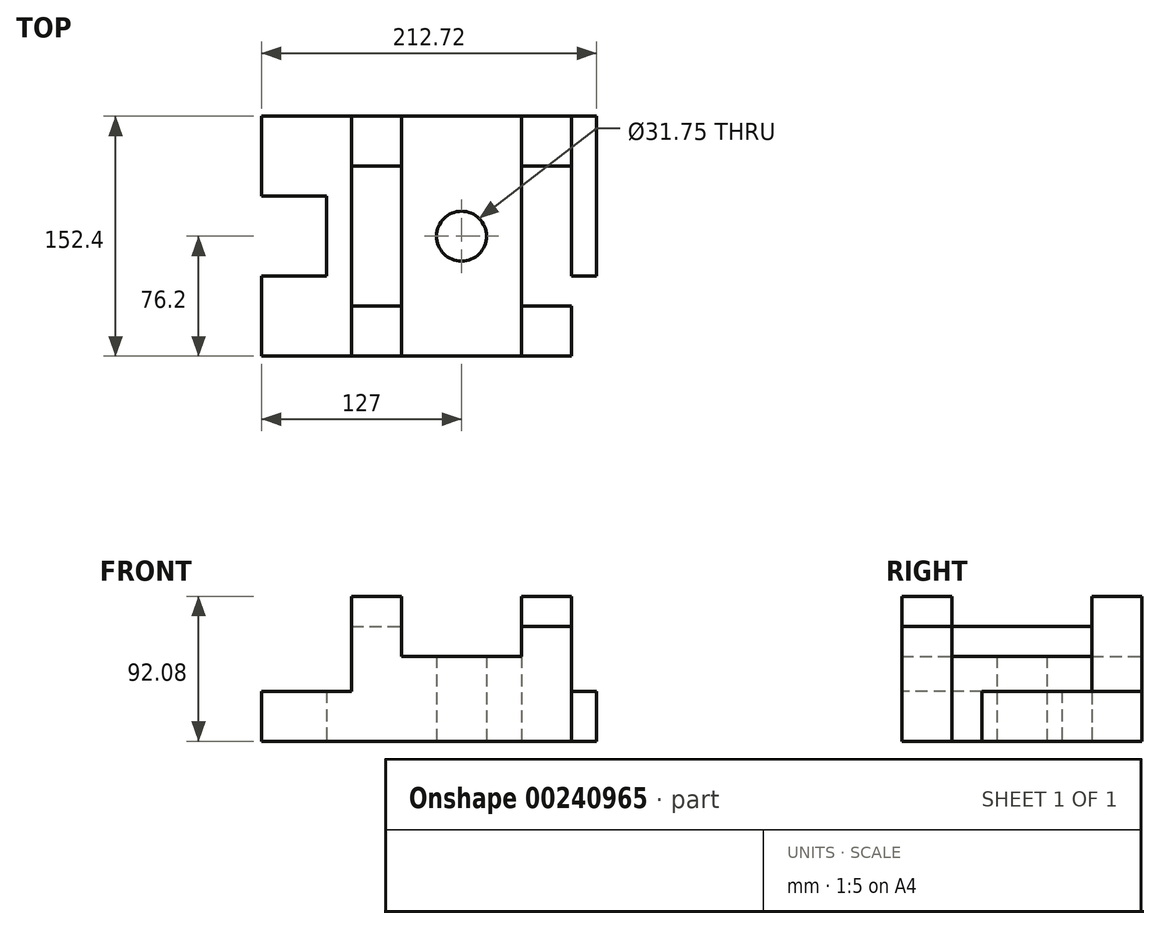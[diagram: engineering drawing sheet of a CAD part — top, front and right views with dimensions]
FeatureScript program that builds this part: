
annotation { "Feature Type Name" : "Feature", "Feature Type Description" : "" }
export const myFeature = defineFeature(function(context is Context, id is Id, definition is map)
    precondition{}
    {
        {
            var Q0;
            Q0=qCreatedBy(makeId("Top.planeOp"),FACE);
            var sketch = newSketch(context, id + "F0", { "sketchPlane" : qUnion([Q0])});
            skLineSegment(sketch, "E0.bottom", {"start": v(-127, 76.2) * mm, "end": v(127, 76.2) * mm});
            skLineSegment(sketch, "E0.top", {"start": v(-127, -76.2) * mm, "end": v(127, -76.2) * mm});
            skLineSegment(sketch, "E0.left", {"start": v(-127, 76.2) * mm, "end": v(-127, -76.2) * mm});
            skLineSegment(sketch, "E0.right", {"start": v(127, 76.2) * mm, "end": v(127, -76.2) * mm});
            skPoint(sketch, "E0.middle", {"position": v(0, 0) * mm});
            skLineSegment(sketch, "E1.bottom", {"start": v(127, -76.2) * mm, "end": v(69.85, -76.2) * mm});
            skLineSegment(sketch, "E1.top", {"start": v(127, -25.4) * mm, "end": v(69.85, -25.4) * mm});
            skLineSegment(sketch, "E1.left", {"start": v(127, -76.2) * mm, "end": v(127, -25.4) * mm});
            skLineSegment(sketch, "E1.right", {"start": v(69.85, -76.2) * mm, "end": v(69.85, -25.4) * mm});
            skLineSegment(sketch, "E2.MirrorCS", {"start": v(85.72, 25.4) * mm, "end": v(85.72, -25.4) * mm});
            skLineSegment(sketch, "E3.MirrorCS", {"start": v(127, 25.1) * mm, "end": v(85.72, 25.4) * mm});
            skLineSegment(sketch, "E4.MirrorCS", {"start": v(127, 25.4) * mm, "end": v(127, -25.4) * mm});
            skLineSegment(sketch, "E5.bottom", {"start": v(85.72, 25.4) * mm, "end": v(69.85, 25.4) * mm});
            skLineSegment(sketch, "E5.top", {"start": v(85.72, 76.2) * mm, "end": v(69.85, 76.2) * mm});
            skLineSegment(sketch, "E5.left", {"start": v(85.72, 25.4) * mm, "end": v(85.72, 76.2) * mm});
            skLineSegment(sketch, "E5.right", {"start": v(69.85, 25.4) * mm, "end": v(69.85, 76.2) * mm});
            skLineSegment(sketch, "E6.MirrorCS", {"start": v(-69.85, 25.4) * mm, "end": v(-69.85, 76.2) * mm});
            skLineSegment(sketch, "E7.MirrorCS", {"start": v(-85.72, 25.4) * mm, "end": v(-69.85, 25.4) * mm});
            skLineSegment(sketch, "E8.MirrorCS", {"start": v(-127, 25.1) * mm, "end": v(-85.72, 25.4) * mm});
            skLineSegment(sketch, "E9.MirrorCS", {"start": v(-85.72, 25.4) * mm, "end": v(-85.72, -25.4) * mm});
            skLineSegment(sketch, "E10.MirrorCS", {"start": v(-127, -25.4) * mm, "end": v(-69.85, -25.4) * mm});
            skLineSegment(sketch, "E11.MirrorCS", {"start": v(-69.85, -76.2) * mm, "end": v(-69.85, -25.4) * mm});
            skLineSegment(sketch, "E12.MirrorCS", {"start": v(-85.72, 25.4) * mm, "end": v(-85.72, 76.2) * mm});
            skLineSegment(sketch, "E13.bottom", {"start": v(69.85, -76.2) * mm, "end": v(38.1, -76.2) * mm});
            skLineSegment(sketch, "E13.top", {"start": v(69.85, -44.45) * mm, "end": v(38.1, -44.45) * mm});
            skLineSegment(sketch, "E13.left", {"start": v(69.85, -76.2) * mm, "end": v(69.85, -44.45) * mm});
            skLineSegment(sketch, "E13.right", {"start": v(38.1, -76.2) * mm, "end": v(38.1, -44.45) * mm});
            skLineSegment(sketch, "E14.MirrorCS", {"start": v(69.85, 44.45) * mm, "end": v(38.1, 44.45) * mm});
            skLineSegment(sketch, "E15.MirrorCS", {"start": v(38.1, 76.2) * mm, "end": v(38.1, 44.45) * mm});
            skLineSegment(sketch, "E16.MirrorCS", {"start": v(-38.1, 76.2) * mm, "end": v(-38.1, 44.45) * mm});
            skLineSegment(sketch, "E17.MirrorCS", {"start": v(-69.85, 44.45) * mm, "end": v(-38.1, 44.45) * mm});
            skLineSegment(sketch, "E18.MirrorCS", {"start": v(-69.85, -44.45) * mm, "end": v(-38.1, -44.45) * mm});
            skLineSegment(sketch, "E19.MirrorCS", {"start": v(-38.1, -76.2) * mm, "end": v(-38.1, -44.45) * mm});
            skLineSegment(sketch, "E20", {"start": v(69.85, 25.4) * mm, "end": v(69.85, -25.4) * mm});
            skLineSegment(sketch, "E21.MirrorCS", {"start": v(-69.85, 25.4) * mm, "end": v(-69.85, -25.4) * mm});
            skLineSegment(sketch, "E22", {"start": v(38.1, 44.45) * mm, "end": v(38.1, -44.45) * mm});
            skLineSegment(sketch, "E23.MirrorCS", {"start": v(-38.1, 44.45) * mm, "end": v(-38.1, -44.45) * mm});
            skCircle(sketch, "E24", {"center": v(0, 0) * mm, "radius": 15.88 * mm});
            skLineSegment(sketch, "E25.bottom", {"start": v(-127, 76.2) * mm, "end": v(-85.72, 76.2) * mm});
            skLineSegment(sketch, "E25.top", {"start": v(-127, 25.4) * mm, "end": v(-85.72, 25.4) * mm});
            skLineSegment(sketch, "E25.left", {"start": v(-127, 76.2) * mm, "end": v(-127, 25.4) * mm});
            skLineSegment(sketch, "E25.right", {"start": v(-85.72, 76.2) * mm, "end": v(-85.72, 25.4) * mm});
            skLineSegment(sketch, "E26.bottom", {"start": v(127, 76.2) * mm, "end": v(85.72, 76.2) * mm});
            skLineSegment(sketch, "E26.top", {"start": v(127, 25.4) * mm, "end": v(85.72, 25.4) * mm});
            skLineSegment(sketch, "E26.left", {"start": v(127, 76.2) * mm, "end": v(127, 25.4) * mm});
            skLineSegment(sketch, "E26.right", {"start": v(85.72, 76.2) * mm, "end": v(85.72, 25.4) * mm});
            skSolve(sketch);
        }
        {
            var Q0;
            {var subQ4=sQuery(id+"F0.wireOp",EDGE,"E0.left");var subQ5=sQuery(id+"F0.wireOp",EDGE,"E0.top");var subQ6=makeQuery(id+"F0.imprint","INTERSECT",VERTEX,{"derivedFrom":[subQ5,subQ4]});Q0=makeQuery(id+"F0.imprint","IMPRINT",FACE,{"disambiguationData":[TD([[makeQuery(id+"F0.imprint","IMPRINT",EDGE,{"disambiguationData":[TD([[subQ6,-1.0]])],"derivedFrom":subQ5}),1.0]])]});}
            var Q1;
            {var subQ0=sQuery(id+"F0.wireOp",EDGE,"E7.MirrorCS");Q1=makeQuery(id+"F0.imprint","IMPRINT",FACE,{"disambiguationData":[TD([[makeQuery(id+"F0.imprint","IMPRINT",EDGE,{"derivedFrom":subQ0}),1.0]])]});}
            var Q2;
            {var subQ1=sQuery(id+"F0.wireOp",EDGE,"E5.bottom");Q2=makeQuery(id+"F0.imprint","IMPRINT",FACE,{"disambiguationData":[TD([[makeQuery(id+"F0.imprint","IMPRINT",EDGE,{"derivedFrom":subQ1}),-1.0]])]});}
            var Q3;
            Q3=makeQuery(id+"F0.imprint","IMPRINT",FACE,{"disambiguationData":[TD([[makeQuery(id+"F0.imprint","IMPRINT",EDGE,{"derivedFrom":sQuery(id+"F0.wireOp",EDGE,"E1.bottom")}),-1.0]])]});
            extrude(context, id + "F1", {"entities" : qUnion([Q0, Q1, Q2, Q3]), "depth" : 31.75 * mm});
        }
        {
            var Q0;
            {var subQ1=sQuery(id+"F0.wireOp",EDGE,"E17.MirrorCS");Q0=makeQuery(id+"F0.imprint","IMPRINT",FACE,{"disambiguationData":[TD([[makeQuery(id+"F0.imprint","IMPRINT",EDGE,{"derivedFrom":subQ1}),-1.0]])]});}
            var Q1;
            Q1=makeQuery(id+"F0.imprint","IMPRINT",FACE,{"disambiguationData":[TD([[makeQuery(id+"F0.imprint","IMPRINT",EDGE,{"derivedFrom":sQuery(id+"F0.wireOp",EDGE,"E1.right")}),1.0]])]});
            extrude(context, id + "F2", {"entities" : qUnion([Q0, Q1]), "operationType" : NewBodyOperationType.ADD, "depth" : 73.02 * mm});
        }
        {
            var Q0;
            {var subQ5=sQuery(id+"F0.wireOp",EDGE,"E12.MirrorCS");Q0=makeQuery(id+"F0.imprint","IMPRINT",FACE,{"disambiguationData":[TD([[makeQuery(id+"F0.imprint","IMPRINT",EDGE,{"derivedFrom":subQ5}),1.0]])]});}
            var Q1;
            Q1=makeQuery(id+"F0.imprint","IMPRINT",FACE,{"disambiguationData":[TD([[makeQuery(id+"F0.imprint","IMPRINT",EDGE,{"derivedFrom":sQuery(id+"F0.wireOp",EDGE,"E26.bottom")}),1.0]])]});
            var Q2;
            {var subQ1=sQuery(id+"F0.wireOp",EDGE,"E6.MirrorCS");var subQ5=sQuery(id+"F0.wireOp",EDGE,"E0.bottom");var subQ6=makeQuery(id+"F0.imprint","INTERSECT",VERTEX,{"derivedFrom":[subQ5,subQ1]});Q2=makeQuery(id+"F0.imprint","IMPRINT",FACE,{"disambiguationData":[TD([[makeQuery(id+"F0.imprint","IMPRINT",EDGE,{"disambiguationData":[TD([[subQ6,1.0]])],"derivedFrom":subQ1}),1.0]])]});}
            var Q3;
            {var subQ3=sQuery(id+"F0.wireOp",EDGE,"E5.bottom");Q3=makeQuery(id+"F0.imprint","IMPRINT",FACE,{"disambiguationData":[TD([[makeQuery(id+"F0.imprint","IMPRINT",EDGE,{"derivedFrom":subQ3}),-1.0]])]});}
            extrude(context, id + "F3", {"entities" : qUnion([Q0, Q1, Q2, Q3]), "operationType" : NewBodyOperationType.ADD, "offsetDistance" : 25.4 * mm, "depth" : 31.75 * mm});
        }
        {
            var Q0;
            {var subQ3=sQuery(id+"F0.wireOp",EDGE,"E16.MirrorCS");Q0=makeQuery(id+"F0.imprint","IMPRINT",FACE,{"disambiguationData":[TD([[makeQuery(id+"F0.imprint","IMPRINT",EDGE,{"derivedFrom":subQ3}),-1.0]])]});}
            var Q1;
            {var subQ4=sQuery(id+"F0.wireOp",EDGE,"E14.MirrorCS");Q1=makeQuery(id+"F0.imprint","IMPRINT",FACE,{"disambiguationData":[TD([[makeQuery(id+"F0.imprint","IMPRINT",EDGE,{"derivedFrom":subQ4}),-1.0]])]});}
            var Q2;
            {var subQ4=sQuery(id+"F0.wireOp",EDGE,"E18.MirrorCS");Q2=makeQuery(id+"F0.imprint","IMPRINT",FACE,{"disambiguationData":[TD([[makeQuery(id+"F0.imprint","IMPRINT",EDGE,{"derivedFrom":subQ4}),-1.0]])]});}
            var Q3;
            Q3=makeQuery(id+"F0.imprint","IMPRINT",FACE,{"disambiguationData":[TD([[makeQuery(id+"F0.imprint","IMPRINT",EDGE,{"derivedFrom":sQuery(id+"F0.wireOp",EDGE,"E13.bottom")}),-1.0]])]});
            extrude(context, id + "F4", {"entities" : qUnion([Q0, Q1, Q2, Q3]), "operationType" : NewBodyOperationType.ADD, "offsetDistance" : 25.4 * mm, "depth" : 92.07 * mm});
        }
        {
            var Q0;
            {var subQ1=sQuery(id+"F0.wireOp",EDGE,"E13.right");Q0=makeQuery(id+"F0.imprint","IMPRINT",FACE,{"disambiguationData":[TD([[makeQuery(id+"F0.imprint","IMPRINT",EDGE,{"derivedFrom":subQ1}),1.0]])]});}
            extrude(context, id + "F5", {"entities" : qUnion([Q0]), "operationType" : NewBodyOperationType.ADD, "depth" : 53.97 * mm});
        }
        {
            var Q0;
            Q0=makeQuery(id+"F1.opExtrude","SWEPT_BODY",BODY,{"disambiguationData":[OSD([sQuery(id+"F0.wireOp",EDGE,"E5.bottom"),sQuery(id+"F0.wireOp",EDGE,"E5.top"),sQuery(id+"F0.wireOp",EDGE,"E5.right"),sQuery(id+"F0.wireOp",EDGE,"E26.right")])]});
            var Q1;
            Q1=makeQuery(id+"F2.opExtrude","SWEPT_BODY",BODY,{"disambiguationData":[OSD([sQuery(id+"F0.wireOp",EDGE,"E1.right"),sQuery(id+"F0.wireOp",EDGE,"E5.right"),sQuery(id+"F0.wireOp",EDGE,"E13.top"),sQuery(id+"F0.wireOp",EDGE,"E14.MirrorCS"),sQuery(id+"F0.wireOp",EDGE,"E20"),sQuery(id+"F0.wireOp",EDGE,"E22")])]});
            var Q2;
            Q2=makeQuery(id+"F2.opExtrude","SWEPT_BODY",BODY,{"disambiguationData":[OSD([sQuery(id+"F0.wireOp",EDGE,"E6.MirrorCS"),sQuery(id+"F0.wireOp",EDGE,"E11.MirrorCS"),sQuery(id+"F0.wireOp",EDGE,"E17.MirrorCS"),sQuery(id+"F0.wireOp",EDGE,"E18.MirrorCS"),sQuery(id+"F0.wireOp",EDGE,"E21.MirrorCS"),sQuery(id+"F0.wireOp",EDGE,"E23.MirrorCS")])]});
            var Q3;
            Q3=makeQuery(id+"F3.opExtrude","SWEPT_BODY",BODY,{"disambiguationData":[OSD([sQuery(id+"F0.wireOp",EDGE,"E5.bottom"),sQuery(id+"F0.wireOp",EDGE,"E5.top"),sQuery(id+"F0.wireOp",EDGE,"E5.right"),sQuery(id+"F0.wireOp",EDGE,"E26.bottom"),sQuery(id+"F0.wireOp",EDGE,"E26.top"),sQuery(id+"F0.wireOp",EDGE,"E26.left")])]});
            var Q4;
            Q4=makeQuery(id+"F4.opExtrude","SWEPT_BODY",BODY,{"disambiguationData":[OSD([sQuery(id+"F0.wireOp",EDGE,"E0.bottom"),sQuery(id+"F0.wireOp",EDGE,"E6.MirrorCS"),sQuery(id+"F0.wireOp",EDGE,"E16.MirrorCS"),sQuery(id+"F0.wireOp",EDGE,"E17.MirrorCS")])]});
            var Q5;
            Q5=makeQuery(id+"F4.opExtrude","SWEPT_BODY",BODY,{"disambiguationData":[OSD([sQuery(id+"F0.wireOp",EDGE,"E0.bottom"),sQuery(id+"F0.wireOp",EDGE,"E5.right"),sQuery(id+"F0.wireOp",EDGE,"E14.MirrorCS"),sQuery(id+"F0.wireOp",EDGE,"E15.MirrorCS")])]});
            var Q6;
            Q6=makeQuery(id+"F4.opExtrude","SWEPT_BODY",BODY,{"disambiguationData":[OSD([sQuery(id+"F0.wireOp",EDGE,"E0.top"),sQuery(id+"F0.wireOp",EDGE,"E11.MirrorCS"),sQuery(id+"F0.wireOp",EDGE,"E18.MirrorCS"),sQuery(id+"F0.wireOp",EDGE,"E19.MirrorCS")])]});
            var Q7;
            Q7=makeQuery(id+"F4.opExtrude","SWEPT_BODY",BODY,{"disambiguationData":[OSD([sQuery(id+"F0.wireOp",EDGE,"E13.bottom"),sQuery(id+"F0.wireOp",EDGE,"E13.top"),sQuery(id+"F0.wireOp",EDGE,"E13.left"),sQuery(id+"F0.wireOp",EDGE,"E13.right")])]});
            var Q8;
            Q8=makeQuery(id+"F5.opExtrude","SWEPT_BODY",BODY,{"disambiguationData":[OSD([sQuery(id+"F0.wireOp",EDGE,"E0.bottom"),sQuery(id+"F0.wireOp",EDGE,"E0.top"),sQuery(id+"F0.wireOp",EDGE,"E13.right"),sQuery(id+"F0.wireOp",EDGE,"E15.MirrorCS"),sQuery(id+"F0.wireOp",EDGE,"E16.MirrorCS"),sQuery(id+"F0.wireOp",EDGE,"E19.MirrorCS"),sQuery(id+"F0.wireOp",EDGE,"E22"),sQuery(id+"F0.wireOp",EDGE,"E23.MirrorCS"),sQuery(id+"F0.wireOp",EDGE,"E24")])]});
            var Q9;
            Q9=makeQuery(id+"F1.opExtrude","SWEPT_BODY",BODY,{"disambiguationData":[OSD([sQuery(id+"F0.wireOp",EDGE,"E0.top"),sQuery(id+"F0.wireOp",EDGE,"E0.left"),sQuery(id+"F0.wireOp",EDGE,"E10.MirrorCS"),sQuery(id+"F0.wireOp",EDGE,"E11.MirrorCS")])]});
            var Q10;
            Q10=makeQuery(id+"F1.opExtrude","SWEPT_BODY",BODY,{"disambiguationData":[OSD([sQuery(id+"F0.wireOp",EDGE,"E1.bottom"),sQuery(id+"F0.wireOp",EDGE,"E1.top"),sQuery(id+"F0.wireOp",EDGE,"E1.left"),sQuery(id+"F0.wireOp",EDGE,"E1.right"),sQuery(id+"F0.wireOp",EDGE,"E13.left")])]});
            var Q11;
            Q11=makeQuery(id+"F1.opExtrude","SWEPT_BODY",BODY,{"disambiguationData":[OSD([sQuery(id+"F0.wireOp",EDGE,"E7.MirrorCS"),sQuery(id+"F0.wireOp",EDGE,"E12.MirrorCS"),sQuery(id+"F0.wireOp",EDGE,"E25.bottom"),sQuery(id+"F0.wireOp",EDGE,"E25.right")])]});
            var Q12;
            Q12=makeQuery(id+"F3.opExtrude","SWEPT_BODY",BODY,{"disambiguationData":[OSD([sQuery(id+"F0.wireOp",EDGE,"E0.bottom"),sQuery(id+"F0.wireOp",EDGE,"E6.MirrorCS"),sQuery(id+"F0.wireOp",EDGE,"E7.MirrorCS"),sQuery(id+"F0.wireOp",EDGE,"E25.right")])]});
            var Q13;
            Q13=makeQuery(id+"F3.opExtrude","SWEPT_BODY",BODY,{"disambiguationData":[OSD([sQuery(id+"F0.wireOp",EDGE,"E9.MirrorCS"),sQuery(id+"F0.wireOp",EDGE,"E12.MirrorCS"),sQuery(id+"F0.wireOp",EDGE,"E25.bottom"),sQuery(id+"F0.wireOp",EDGE,"E25.top"),sQuery(id+"F0.wireOp",EDGE,"E25.left")])]});
            var Q14;
            Q14=qCreatedBy(makeId("Origin.pointOp"),VERTEX);
            transform(context, id + "F6", {"entities" : qUnion([Q0, Q1, Q2, Q3, Q4, Q5, Q6, Q7, Q8, Q9, Q10, Q11, Q12, Q13]), "transformType" : TransformType.SCALE_UNIFORMLY, "scale" : 1, "scalePoint" : qUnion([Q14]), "makeCopy" : false});
        }
        {
            var Q0;
            {var subQ0=sQuery(id+"F0.wireOp",EDGE,"E21.MirrorCS");Q0=makeQuery(id+"F0.imprint","IMPRINT",FACE,{"disambiguationData":[TD([[makeQuery(id+"F0.imprint","IMPRINT",EDGE,{"derivedFrom":subQ0}),-1.0]])]});}
            extrude(context, id + "F7", {"entities" : qUnion([Q0]), "operationType" : NewBodyOperationType.ADD, "depth" : 31.75 * mm});
        }
        {
            var Q0;
            {var subQ0=sQuery(id+"F0.wireOp",EDGE,"E5.bottom");Q0=makeQuery(id+"F0.imprint","IMPRINT",FACE,{"disambiguationData":[TD([[makeQuery(id+"F0.imprint","IMPRINT",EDGE,{"derivedFrom":subQ0}),1.0]])]});}
            extrude(context, id + "F8", {"entities" : qUnion([Q0]), "operationType" : NewBodyOperationType.ADD, "depth" : 31.75 * mm});
        }
    });
